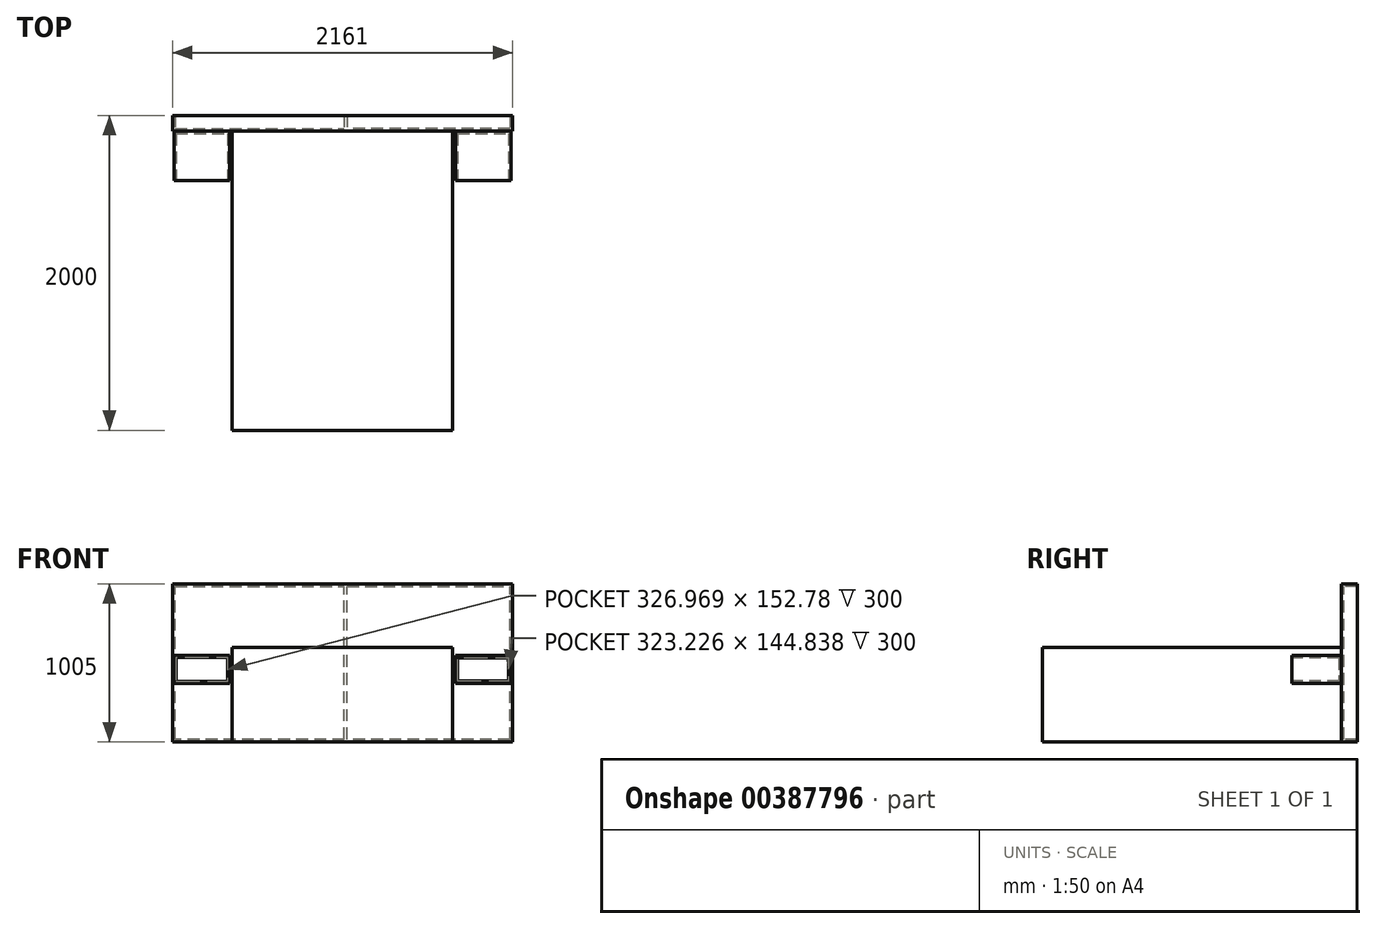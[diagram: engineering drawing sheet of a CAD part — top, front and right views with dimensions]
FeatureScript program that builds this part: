
annotation { "Feature Type Name" : "Feature", "Feature Type Description" : "" }
export const myFeature = defineFeature(function(context is Context, id is Id, definition is map)
    precondition{}
    {
        {
            var Q0;
            Q0=qCreatedBy(makeId("Front.planeOp"),FACE);
            var sketch = newSketch(context, id + "F0", { "sketchPlane" : qUnion([Q0])});
            skLineSegment(sketch, "E0.bottom", {"start": v(0, 989) * mm, "end": v(2161, 989) * mm});
            skLineSegment(sketch, "E0.top", {"start": v(0, 0) * mm, "end": v(2161, 0) * mm});
            skLineSegment(sketch, "E0.left", {"start": v(0, 989) * mm, "end": v(0, 0) * mm});
            skLineSegment(sketch, "E0.right", {"start": v(2161, 989) * mm, "end": v(2161, 0) * mm});
            skSolve(sketch);
        }
        {
            var Q0;
            Q0 = qSketchRegion(id + "F0", true);
            var Q1;
            Q1=makeQuery(id+"F0.imprint","IMPRINT",FACE,{"disambiguationData":[TD([[makeQuery(id+"F0.imprint","IMPRINT",EDGE,{"derivedFrom":sQuery(id+"F0.wireOp",EDGE,"E0.bottom")}),-1.0]])]});
            extrude(context, id + "F1", {"entities" : qUnion([Q0, Q1]), "depth" : 16 * mm});
        }
        {
            var Q0;
            Q0=makeQuery(id+"F1.opExtrude","CAP_FACE",FACE,{"disambiguationData":[OSD([sQuery(id+"F0.wireOp",EDGE,"E0.bottom"),sQuery(id+"F0.wireOp",EDGE,"E0.top"),sQuery(id+"F0.wireOp",EDGE,"E0.left"),sQuery(id+"F0.wireOp",EDGE,"E0.right")])],"isStart":false});
            var sketch = newSketch(context, id + "F2", { "sketchPlane" : qUnion([Q0])});
            skLineSegment(sketch, "E1.bottom", {"start": v(380.5, 600) * mm, "end": v(1780.5, 600) * mm});
            skLineSegment(sketch, "E1.top", {"start": v(380.5, 0) * mm, "end": v(1780.5, 0) * mm});
            skLineSegment(sketch, "E1.left", {"start": v(380.5, 600) * mm, "end": v(380.5, 0) * mm});
            skLineSegment(sketch, "E1.right", {"start": v(1780.5, 600) * mm, "end": v(1780.5, 0) * mm});
            skLineSegment(sketch, "E2", {"start": v(1080.5, 0) * mm, "end": v(1080.5, 989) * mm, "construction": true});
            skSolve(sketch);
        }
        {
            var Q0;
            Q0 = qSketchRegion(id + "F2", true);
            extrude(context, id + "F3", {"entities" : qUnion([Q0]), "operationType" : NewBodyOperationType.ADD, "depth" : 1900 * mm});
        }
        {
            var Q0;
            Q0=makeQuery(id+"F1.opExtrude","CAP_FACE",FACE,{"disambiguationData":[OSD([sQuery(id+"F0.wireOp",EDGE,"E0.bottom"),sQuery(id+"F0.wireOp",EDGE,"E0.top"),sQuery(id+"F0.wireOp",EDGE,"E0.left"),sQuery(id+"F0.wireOp",EDGE,"E0.right")])],"isStart":false});
            var sketch = newSketch(context, id + "F4", { "sketchPlane" : qUnion([Q0])});
            skLineSegment(sketch, "E3.bottom", {"start": v(10, 550) * mm, "end": v(362, 550) * mm});
            skLineSegment(sketch, "E3.top", {"start": v(10, 374) * mm, "end": v(362, 374) * mm});
            skLineSegment(sketch, "E3.left", {"start": v(10, 550) * mm, "end": v(10, 374) * mm});
            skLineSegment(sketch, "E3.right", {"start": v(362, 550) * mm, "end": v(362, 374) * mm});
            skLineSegment(sketch, "E4.bottom", {"start": v(1799, 550) * mm, "end": v(2151, 550) * mm});
            skLineSegment(sketch, "E4.top", {"start": v(1799, 374) * mm, "end": v(2151, 374) * mm});
            skLineSegment(sketch, "E4.left", {"start": v(1799, 550) * mm, "end": v(1799, 374) * mm});
            skLineSegment(sketch, "E4.right", {"start": v(2151, 550) * mm, "end": v(2151, 374) * mm});
            skSolve(sketch);
        }
        {
            var Q0;
            Q0 = qSketchRegion(id + "F4", true);
            var Q1;
            Q1 = qSketchRegion(id + "F6", true);
            var Q2;
            Q2 = qSketchRegion(id + "F8", true);
            extrude(context, id + "F5", {"entities" : qUnion([Q0, Q1, Q2]), "operationType" : NewBodyOperationType.ADD, "depth" : 315 * mm});
        }
        {
            var Q0;
            Q0=makeQuery(id+"F1.opExtrude","CAP_FACE",FACE,{"disambiguationData":[OSD([sQuery(id+"F0.wireOp",EDGE,"E0.bottom"),sQuery(id+"F0.wireOp",EDGE,"E0.top"),sQuery(id+"F0.wireOp",EDGE,"E0.left"),sQuery(id+"F0.wireOp",EDGE,"E0.right")])],"isStart":false});
            var sketch = newSketch(context, id + "F6", { "sketchPlane" : qUnion([Q0])});
            skLineSegment(sketch, "E5.bottom", {"start": v(0, 989) * mm, "end": v(2161, 989) * mm});
            skLineSegment(sketch, "E5.top", {"start": v(0, 1005) * mm, "end": v(2161, 1005) * mm});
            skLineSegment(sketch, "E5.left", {"start": v(0, 989) * mm, "end": v(0, 1005) * mm});
            skLineSegment(sketch, "E5.right", {"start": v(2161, 989) * mm, "end": v(2161, 1005) * mm});
            skSolve(sketch);
        }
        {
            var Q0;
            Q0 = qSketchRegion(id + "F6", true);
            extrude(context, id + "F7", {"entities" : qUnion([Q0]), "operationType" : NewBodyOperationType.ADD, "oppositeDirection" : true, "depth" : 100 * mm});
        }
        {
            var Q0;
            Q0=makeQuery(id+"F1.opExtrude","CAP_FACE",FACE,{"disambiguationData":[OSD([sQuery(id+"F0.wireOp",EDGE,"E0.bottom"),sQuery(id+"F0.wireOp",EDGE,"E0.top"),sQuery(id+"F0.wireOp",EDGE,"E0.left"),sQuery(id+"F0.wireOp",EDGE,"E0.right")])],"isStart":true});
            var sketch = newSketch(context, id + "F8", { "sketchPlane" : qUnion([Q0])});
            skLineSegment(sketch, "E6.bottom", {"start": v(-2161, 0) * mm, "end": v(0, 0) * mm});
            skLineSegment(sketch, "E6.top", {"start": v(-2161, 18) * mm, "end": v(0, 18) * mm});
            skLineSegment(sketch, "E6.left", {"start": v(-2161, 0) * mm, "end": v(-2161, 18) * mm});
            skLineSegment(sketch, "E6.right", {"start": v(0, 0) * mm, "end": v(0, 18) * mm});
            skLineSegment(sketch, "E7.bottom", {"start": v(-1496.52, 18) * mm, "end": v(-1478.52, 18) * mm});
            skLineSegment(sketch, "E7.top", {"start": v(-1496.52, 989) * mm, "end": v(-1478.52, 989) * mm});
            skLineSegment(sketch, "E8.bottom", {"start": v(-1109.65, 18) * mm, "end": v(-1091.65, 18) * mm});
            skLineSegment(sketch, "E8.top", {"start": v(-1109.65, 989) * mm, "end": v(-1091.65, 989) * mm});
            skLineSegment(sketch, "E8.left", {"start": v(-1109.65, 18) * mm, "end": v(-1109.65, 989) * mm});
            skLineSegment(sketch, "E8.right", {"start": v(-1091.65, 18) * mm, "end": v(-1091.65, 989) * mm});
            skLineSegment(sketch, "E9.bottom", {"start": v(-2161, 18) * mm, "end": v(-2143, 18) * mm});
            skLineSegment(sketch, "E9.top", {"start": v(-2161, 989) * mm, "end": v(-2143, 989) * mm});
            skLineSegment(sketch, "E9.left", {"start": v(-2161, 18) * mm, "end": v(-2161, 989) * mm});
            skLineSegment(sketch, "E9.right", {"start": v(-2143, 18) * mm, "end": v(-2143, 989) * mm});
            skLineSegment(sketch, "E10.bottom", {"start": v(0, 18) * mm, "end": v(-18, 18) * mm});
            skLineSegment(sketch, "E10.top", {"start": v(0, 989) * mm, "end": v(-18, 989) * mm});
            skLineSegment(sketch, "E10.left", {"start": v(0, 18) * mm, "end": v(0, 989) * mm});
            skLineSegment(sketch, "E10.right", {"start": v(-18, 18) * mm, "end": v(-18, 989) * mm});
            skSolve(sketch);
        }
        {
            var Q0;
            Q0 = qSketchRegion(id + "F8", true);
            extrude(context, id + "F9", {"entities" : qUnion([Q0]), "operationType" : NewBodyOperationType.ADD, "depth" : 84 * mm});
        }
        {
            var Q0;
            Q0=makeQuery(id+"F5.opExtrude","CAP_FACE",FACE,{"disambiguationData":[OSD([sQuery(id+"F4.wireOp",EDGE,"E3.bottom"),sQuery(id+"F4.wireOp",EDGE,"E3.top"),sQuery(id+"F4.wireOp",EDGE,"E3.left"),sQuery(id+"F4.wireOp",EDGE,"E3.right")])],"isStart":false});
            var sketch = newSketch(context, id + "F10", { "sketchPlane" : qUnion([Q0])});
            skSolve(sketch);
        }
        {
            var Q0;
            Q0=makeQuery(id+"F10.imprint","IMPRINT",FACE,{"disambiguationData":[TD([[makeQuery(id+"F10.imprint","IMPRINT",EDGE,{"derivedFrom":makeQuery(id+"F5.opExtrude","CAP_EDGE",EDGE,{"disambiguationData":[OSD([sQuery(id+"F4.wireOp",EDGE,"E3.bottom")])],"isStart":false})}),-1.0]])]});
            var sketch = newSketch(context, id + "F11", { "sketchPlane" : qUnion([Q0])});
            skLineSegment(sketch, "E11.bottom", {"start": v(22.74, 538.44) * mm, "end": v(349.71, 538.44) * mm});
            skLineSegment(sketch, "E11.top", {"start": v(22.74, 385.66) * mm, "end": v(349.71, 385.66) * mm});
            skLineSegment(sketch, "E11.left", {"start": v(22.74, 538.44) * mm, "end": v(22.74, 385.66) * mm});
            skLineSegment(sketch, "E11.right", {"start": v(349.71, 538.44) * mm, "end": v(349.71, 385.66) * mm});
            skSolve(sketch);
        }
        {
            var Q0;
            Q0=makeQuery(id+"F11.imprint","IMPRINT",FACE,{"disambiguationData":[TD([[makeQuery(id+"F11.imprint","IMPRINT",EDGE,{"derivedFrom":sQuery(id+"F11.wireOp",EDGE,"E11.bottom")}),-1.0]])]});
            extrude(context, id + "F12", {"entities" : qUnion([Q0]), "operationType" : NewBodyOperationType.REMOVE, "oppositeDirection" : true, "depth" : 300 * mm});
        }
        {
            var Q0;
            Q0=makeQuery(id+"F5.opExtrude","CAP_FACE",FACE,{"disambiguationData":[OSD([sQuery(id+"F4.wireOp",EDGE,"E4.bottom"),sQuery(id+"F4.wireOp",EDGE,"E4.top"),sQuery(id+"F4.wireOp",EDGE,"E4.left"),sQuery(id+"F4.wireOp",EDGE,"E4.right")])],"isStart":false});
            var sketch = newSketch(context, id + "F13", { "sketchPlane" : qUnion([Q0])});
            skLineSegment(sketch, "E12.bottom", {"start": v(1811.48, 534.41) * mm, "end": v(2134.71, 534.41) * mm});
            skLineSegment(sketch, "E12.top", {"start": v(1811.48, 389.57) * mm, "end": v(2134.71, 389.57) * mm});
            skLineSegment(sketch, "E12.left", {"start": v(1811.48, 534.41) * mm, "end": v(1811.48, 389.57) * mm});
            skLineSegment(sketch, "E12.right", {"start": v(2134.71, 534.41) * mm, "end": v(2134.71, 389.57) * mm});
            skSolve(sketch);
        }
        {
            var Q0;
            Q0 = qSketchRegion(id + "F13", true);
            extrude(context, id + "F14", {"entities" : qUnion([Q0]), "operationType" : NewBodyOperationType.REMOVE, "oppositeDirection" : true, "depth" : 300 * mm});
        }
    });
